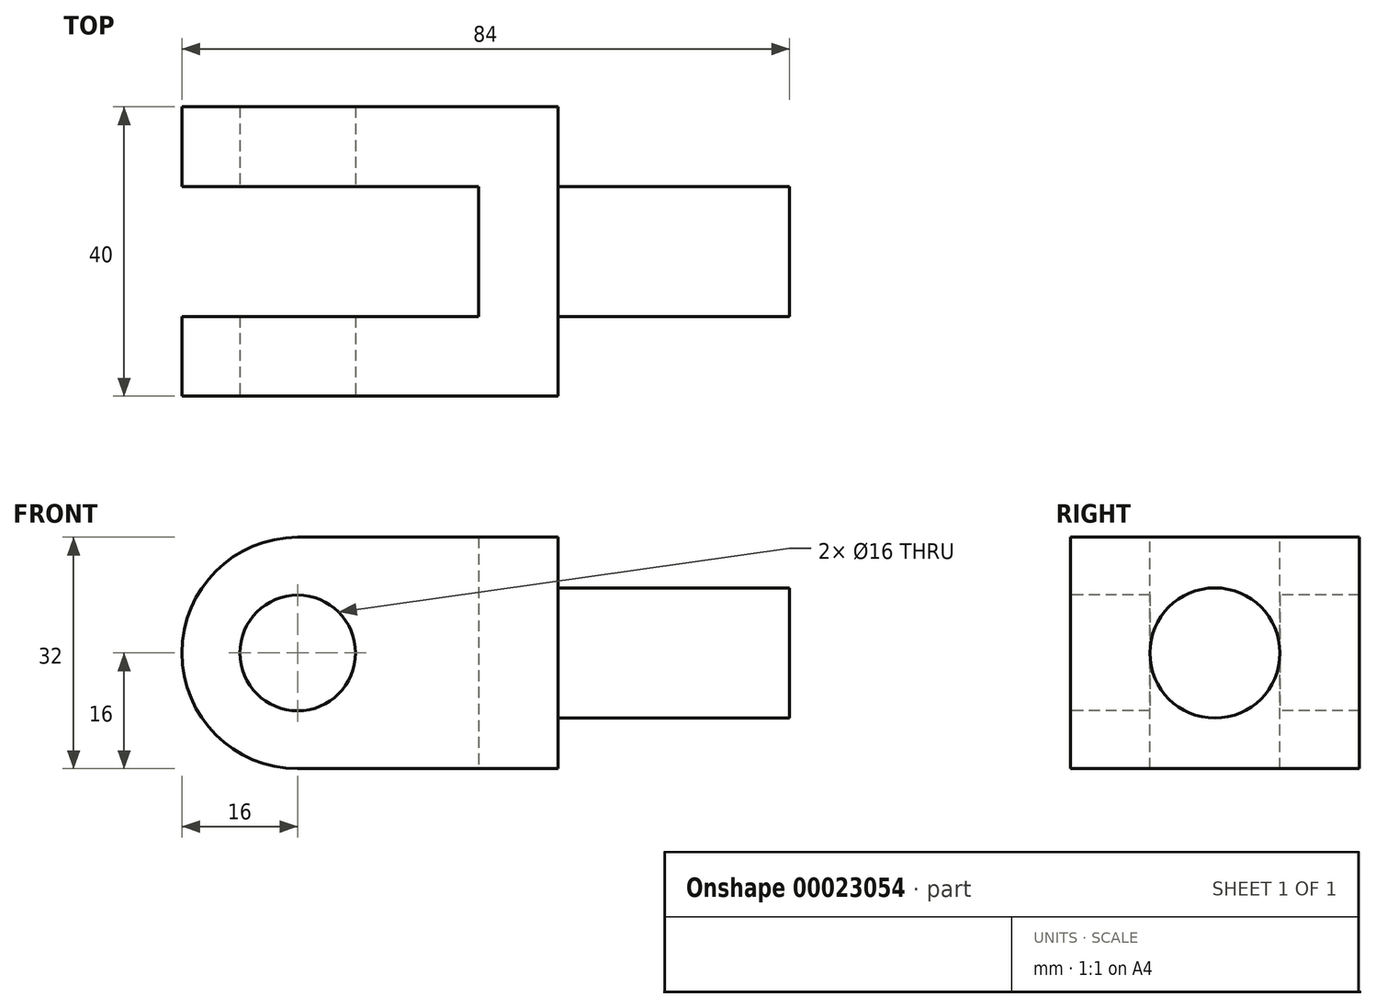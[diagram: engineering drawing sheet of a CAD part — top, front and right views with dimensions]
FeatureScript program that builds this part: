
annotation { "Feature Type Name" : "Feature", "Feature Type Description" : "" }
export const myFeature = defineFeature(function(context is Context, id is Id, definition is map)
    precondition{}
    {
        {
            var Q0;
            Q0=qCreatedBy(makeId("Top.planeOp"),FACE);
            var sketch = newSketch(context, id + "F0", { "sketchPlane" : qUnion([Q0])});
            skLineSegment(sketch, "E0.bottom", {"start": v(0, 0) * mm, "end": v(52, 0) * mm});
            skLineSegment(sketch, "E0.top", {"start": v(0, -11) * mm, "end": v(41, -11) * mm});
            skLineSegment(sketch, "E0.left", {"start": v(0, 0) * mm, "end": v(0, -11) * mm});
            skLineSegment(sketch, "E0.right", {"start": v(52, 0) * mm, "end": v(52, -11) * mm});
            skLineSegment(sketch, "E1.bottom", {"start": v(0, -29) * mm, "end": v(41, -29) * mm});
            skLineSegment(sketch, "E1.top", {"start": v(0, -40) * mm, "end": v(52, -40) * mm});
            skLineSegment(sketch, "E1.left", {"start": v(0, -29) * mm, "end": v(0, -40) * mm});
            skLineSegment(sketch, "E1.right", {"start": v(52, -29) * mm, "end": v(52, -40) * mm});
            skLineSegment(sketch, "E2", {"start": v(41, -11) * mm, "end": v(41, -29) * mm});
            skLineSegment(sketch, "E3", {"start": v(52, -11) * mm, "end": v(52, -29) * mm});
            skSolve(sketch);
        }
        {
            var Q0;
            Q0 = qSketchRegion(id + "F0", true);
            extrude(context, id + "F1", {"entities" : qUnion([Q0]), "depth" : 32 * mm});
        }
        {
            var Q0;
            Q0=makeQuery(id+"F1.opExtrude","SWEPT_FACE",FACE,{"disambiguationData":[OSD([sQuery(id+"F0.wireOp",EDGE,"E1.top")])]});
            var sketch = newSketch(context, id + "F2", { "sketchPlane" : qUnion([Q0])});
            skLineSegment(sketch, "E4", {"start": v(52, 16) * mm, "end": v(16, 16) * mm, "construction": true});
            skCircle(sketch, "E5", {"center": v(16, 16) * mm, "radius": 16 * mm});
            skSolve(sketch);
        }
        {
            var Q0;
            Q0=sQuery(id+"F2.wireOp",VERTEX,"E5.center");
            var Q1;
            Q1=makeQuery(id+"F1.opExtrude","SWEPT_BODY",BODY,{"disambiguationData":[OSD([sQuery(id+"F0.wireOp",EDGE,"E0.bottom"),sQuery(id+"F0.wireOp",EDGE,"E0.top"),sQuery(id+"F0.wireOp",EDGE,"E0.left"),sQuery(id+"F0.wireOp",EDGE,"E0.right"),sQuery(id+"F0.wireOp",EDGE,"E1.bottom"),sQuery(id+"F0.wireOp",EDGE,"E1.top"),sQuery(id+"F0.wireOp",EDGE,"E1.left"),sQuery(id+"F0.wireOp",EDGE,"E1.right"),sQuery(id+"F0.wireOp",EDGE,"E2"),sQuery(id+"F0.wireOp",EDGE,"E3")])]});
            hole(context, id + "F3", {"style" : HoleStyle.SIMPLE, "holeDiameter" : 16 * mm, "endStyle" : HoleEndStyle.THROUGH, "locations" : qUnion([Q0]), "scope" : qUnion([Q1])});
        }
        {
            var Q0;
            Q0=makeQuery(id+"F1.opExtrude","SWEPT_FACE",FACE,{"disambiguationData":[OSD([sQuery(id+"F0.wireOp",EDGE,"E0.right"),sQuery(id+"F0.wireOp",EDGE,"E1.right"),sQuery(id+"F0.wireOp",EDGE,"E3")])]});
            var sketch = newSketch(context, id + "F4", { "sketchPlane" : qUnion([Q0])});
            skLineSegment(sketch, "E6", {"start": v(-40, 32) * mm, "end": v(0, 0) * mm, "construction": true});
            skLineSegment(sketch, "E7", {"start": v(-40, 0) * mm, "end": v(0, 32) * mm, "construction": true});
            skCircle(sketch, "E8", {"center": v(-20, 16) * mm, "radius": 9 * mm});
            skSolve(sketch);
        }
        {
            var Q0;
            Q0 = qSketchRegion(id + "F4", true);
            extrude(context, id + "F5", {"entities" : qUnion([Q0]), "operationType" : NewBodyOperationType.ADD, "depth" : 32 * mm});
        }
        {
            var Q0;
            {var subQ0=sQuery(id+"F0.wireOp",EDGE,"E1.top");var subQ1=makeQuery(id+"F1.opExtrude","CAP_EDGE",EDGE,{"disambiguationData":[OSD([subQ0])],"isStart":false});var subQ2=sQuery(id+"F2.wireOp",EDGE,"E5");var subQ3=makeQuery(id+"F2.imprint","INTERSECT",VERTEX,{"derivedFrom":[subQ1,subQ2]});Q0=makeQuery(id+"F2.imprint","IMPRINT",FACE,{"disambiguationData":[TD([[makeQuery(id+"F2.imprint","IMPRINT",EDGE,{"disambiguationData":[TD([[subQ3,-1.0]])],"derivedFrom":subQ2}),-1.0]])]});}
            var Q1;
            {var subQ0=sQuery(id+"F0.wireOp",EDGE,"E1.top");var subQ2=sQuery(id+"F2.wireOp",EDGE,"E5");var subQ4=makeQuery(id+"F1.opExtrude","CAP_EDGE",EDGE,{"disambiguationData":[OSD([subQ0])],"isStart":true});var subQ6=makeQuery(id+"F2.imprint","INTERSECT",VERTEX,{"derivedFrom":[subQ4,subQ2]});Q1=makeQuery(id+"F2.imprint","IMPRINT",FACE,{"disambiguationData":[TD([[makeQuery(id+"F2.imprint","IMPRINT",EDGE,{"disambiguationData":[TD([[subQ6,1.0]])],"derivedFrom":subQ2}),-1.0]])]});}
            extrude(context, id + "F6", {"entities" : qUnion([Q0, Q1]), "operationType" : NewBodyOperationType.REMOVE, "endBound" : BoundingType.THROUGH_ALL, "oppositeDirection" : true, "depth" : 25 * mm});
        }
    });
